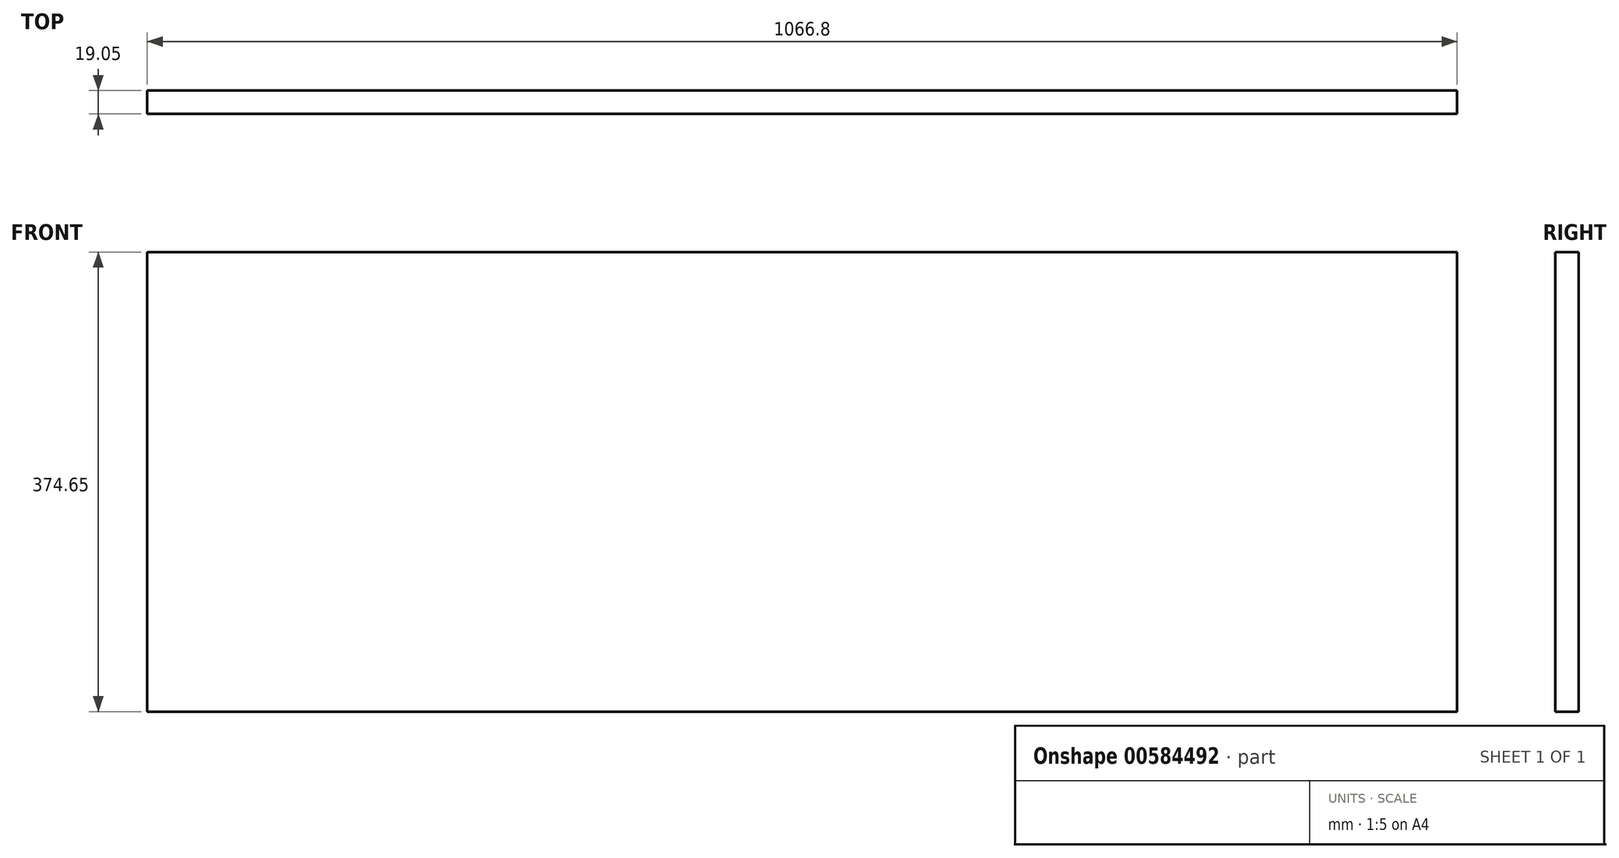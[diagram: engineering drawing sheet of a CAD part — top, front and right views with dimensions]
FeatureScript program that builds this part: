
annotation { "Feature Type Name" : "Feature", "Feature Type Description" : "" }
export const myFeature = defineFeature(function(context is Context, id is Id, definition is map)
    precondition{}
    {
        {
            var Q0;
            Q0=qCreatedBy(makeId("Front.planeOp"),FACE);
            var sketch = newSketch(context, id + "F0", { "sketchPlane" : qUnion([Q0])});
            skLineSegment(sketch, "E0.bottom", {"start": v(0, 0) * mm, "end": v(1066.8, 0) * mm});
            skLineSegment(sketch, "E0.top", {"start": v(0, 374.65) * mm, "end": v(1066.8, 374.65) * mm});
            skLineSegment(sketch, "E0.left", {"start": v(0, 0) * mm, "end": v(0, 374.65) * mm});
            skLineSegment(sketch, "E0.right", {"start": v(1066.8, 0) * mm, "end": v(1066.8, 374.65) * mm});
            skSolve(sketch);
        }
        {
            var Q0;
            Q0=makeQuery(id+"F0.imprint","IMPRINT",FACE,{"disambiguationData":[TD([[makeQuery(id+"F0.imprint","IMPRINT",EDGE,{"derivedFrom":sQuery(id+"F0.wireOp",EDGE,"E0.bottom")}),1.0]])]});
            extrude(context, id + "F1", {"entities" : qUnion([Q0]), "depth" : 19.05 * mm, "offsetDistance" : 25.4 * mm});
        }
    });
